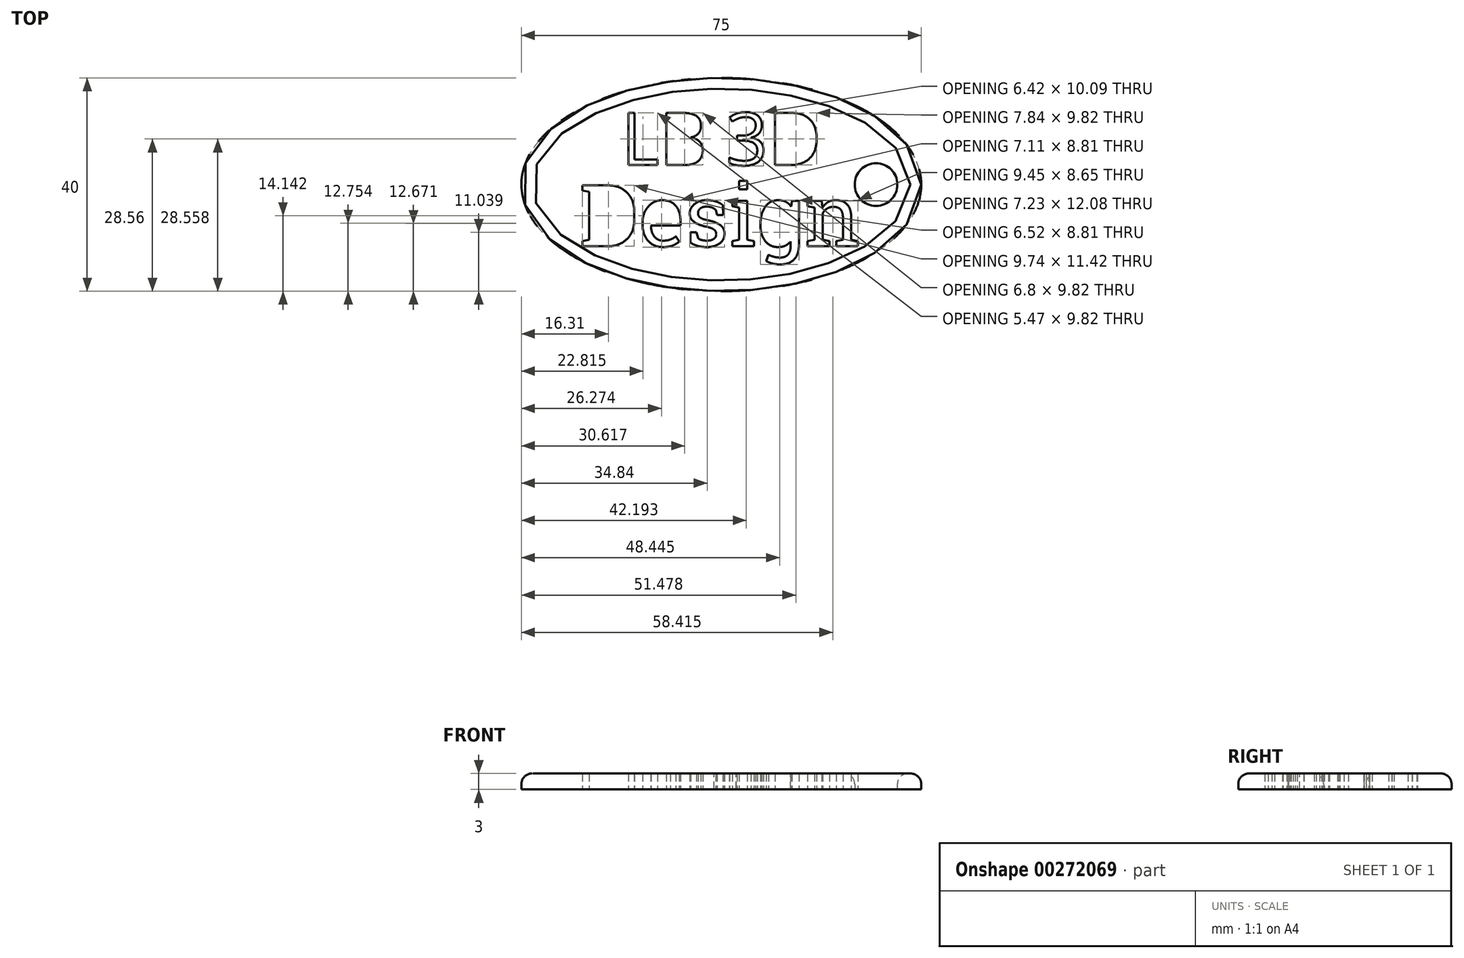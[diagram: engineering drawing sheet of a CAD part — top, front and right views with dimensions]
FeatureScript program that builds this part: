
annotation { "Feature Type Name" : "Feature", "Feature Type Description" : "" }
export const myFeature = defineFeature(function(context is Context, id is Id, definition is map)
    precondition{}
    {
        {
            var Q0;
            Q0=qCreatedBy(makeId("Top.planeOp"),FACE);
            var sketch = newSketch(context, id + "F0", { "sketchPlane" : qUnion([Q0])});
            skEllipse(sketch, "E0", {"center": v(0, 0) * mm, "majorRadius": 37.5 * mm, "minorRadius": 20 * mm, "majorAxis": v(1, 0)});
            skPoint(sketch, "E1.centerSnap0", {"position": v(37.5, 0) * mm});
            skCircle(sketch, "E2", {"center": v(29.03, 0) * mm, "radius": 4 * mm});
            skText(sketch, "E3", { "text": "LB 3D", "fontName": "OpenSans-Regular.ttf"});
            skText(sketch, "E4", { "text": "Design", "fontName": "RobotoSlab-Regular.ttf"});
            const initialGuessF0  = {"E3": [-0.01877, 0.00365, 1, 0, 0.0099], "E4": [-0.02662, -0.01157, 1, 0, 0.01157]};
            skSetInitialGuess(sketch, initialGuessF0);
            skSolve(sketch);
        }
        {
            var Q0;
            Q0=makeQuery(id+"F0.imprint","IMPRINT",FACE,{"disambiguationData":[TD([[makeQuery(id+"F0.imprint","IMPRINT",EDGE,{"derivedFrom":sQuery(id+"F0.wireOp",EDGE,"E0")}),1.0]])]});
            extrude(context, id + "F1", {"entities" : qUnion([Q0]), "depth" : 3 * mm});
        }
        {
            var Q0;
            Q0=makeQuery(id+"F1.opExtrude","CAP_EDGE",EDGE,{"disambiguationData":[OSD([sQuery(id+"F0.wireOp",EDGE,"E0")])],"isStart":false});
            var Q1;
            Q1=makeQuery(id+"F1.opExtrude","CAP_EDGE",EDGE,{"disambiguationData":[OSD([sQuery(id+"F0.wireOp",EDGE,"E2")])],"isStart":false});
            fillet(context, id + "F2", {"entities" : qUnion([Q0, Q1]), "radius" : 2 * mm, "tangentPropagation" : true, "allowEdgeOverflow" : false});
        }
    });
